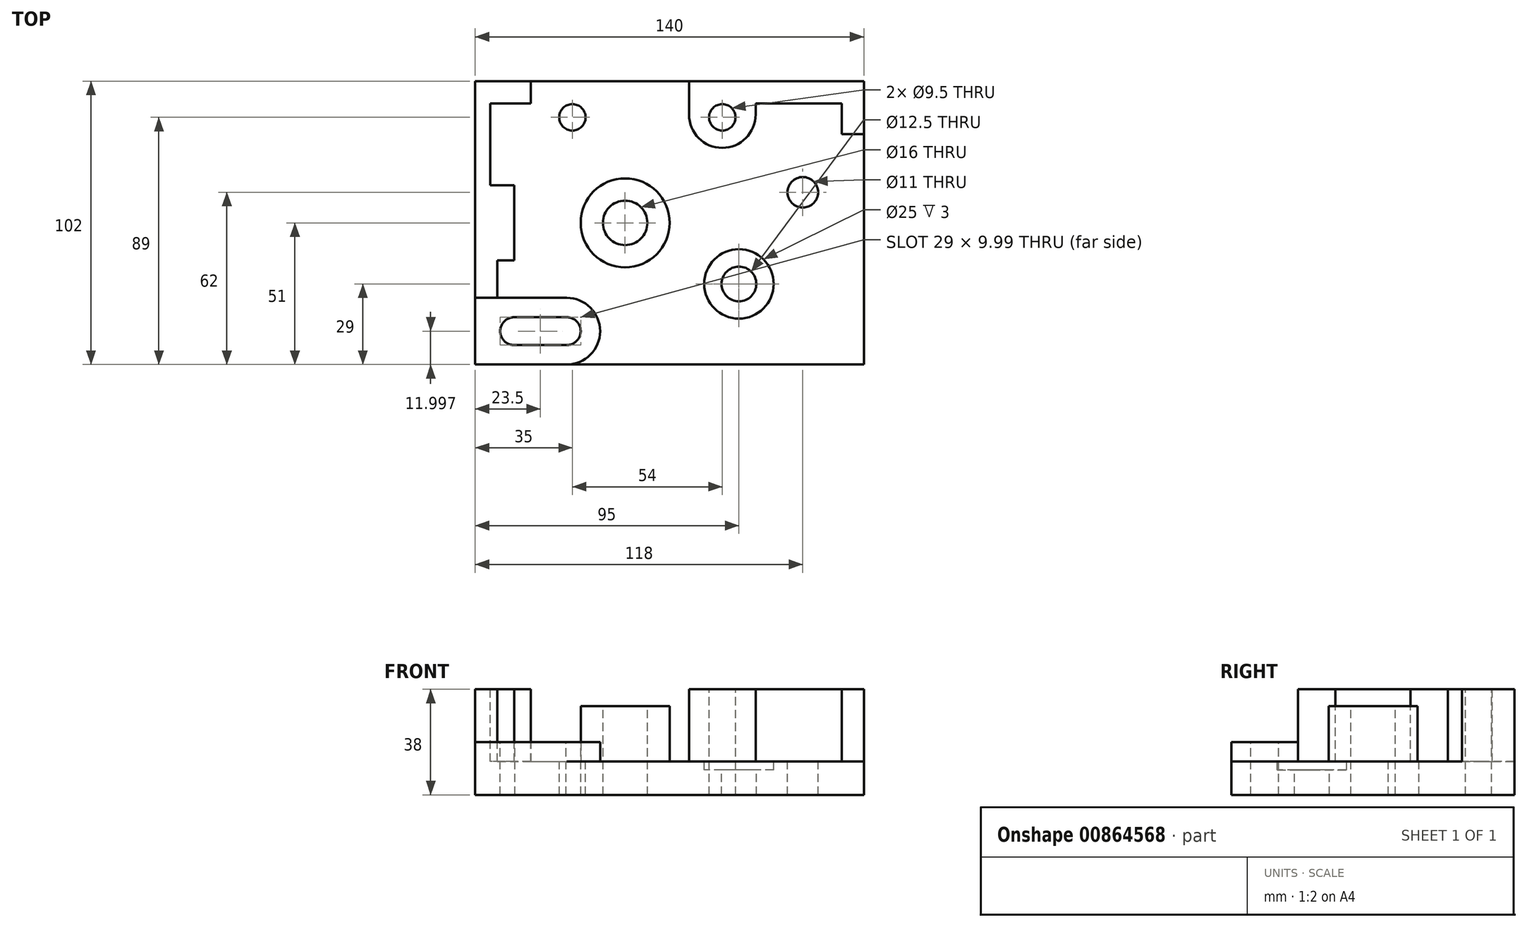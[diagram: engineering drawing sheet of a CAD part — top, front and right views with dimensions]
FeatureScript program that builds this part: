
annotation { "Feature Type Name" : "Feature", "Feature Type Description" : "" }
export const myFeature = defineFeature(function(context is Context, id is Id, definition is map)
    precondition{}
    {
        {
            var Q0;
            Q0=qCreatedBy(makeId("Front.planeOp"),FACE);
            var sketch = newSketch(context, id + "F0", { "sketchPlane" : qUnion([Q0])});
            skLineSegment(sketch, "E0.bottom", {"start": v(0, 0) * mm, "end": v(140, 0) * mm});
            skLineSegment(sketch, "E0.top", {"start": v(0, 38) * mm, "end": v(140, 38) * mm});
            skLineSegment(sketch, "E0.left", {"start": v(0, 0) * mm, "end": v(0, 38) * mm});
            skLineSegment(sketch, "E0.right", {"start": v(140, 0) * mm, "end": v(140, 38) * mm});
            skSolve(sketch);
        }
        {
            var Q0;
            Q0=qSketchRegion(id+"F0",true);
            extrude(context, id + "F1", {"entities" : qUnion([Q0]), "depth" : 102 * mm, "offsetDistance" : 25.4 * mm});
        }
        {
            var Q0;
            Q0=makeQuery(id+"F1.opExtrude","SWEPT_FACE",FACE,{"disambiguationData":[OSD([sQuery(id+"F0.wireOp",EDGE,"E0.top")])]});
            var sketch = newSketch(context, id + "F2", { "sketchPlane" : qUnion([Q0])});
            skCircle(sketch, "E1", {"center": v(35, -13) * mm, "radius": 4.75 * mm});
            skCircle(sketch, "E2", {"center": v(89, -13) * mm, "radius": 4.75 * mm});
            skSolve(sketch);
        }
        {
            var Q0;
            Q0=qSketchRegion(id+"F2",true);
            extrude(context, id + "F3", {"entities" : qUnion([Q0]), "operationType" : NewBodyOperationType.REMOVE, "oppositeDirection" : true, "depth" : 40 * mm, "offsetDistance" : 25.4 * mm});
        }
        {
            var Q0;
            Q0=makeQuery(id+"F1.opExtrude","SWEPT_FACE",FACE,{"disambiguationData":[OSD([sQuery(id+"F0.wireOp",EDGE,"E0.top")])]});
            var sketch = newSketch(context, id + "F4", { "sketchPlane" : qUnion([Q0])});
            skCircle(sketch, "E3", {"center": v(54, -51) * mm, "radius": 8 * mm});
            skSolve(sketch);
        }
        {
            var Q0;
            Q0=qSketchRegion(id+"F4",true);
            extrude(context, id + "F5", {"entities" : qUnion([Q0]), "operationType" : NewBodyOperationType.REMOVE, "oppositeDirection" : true, "depth" : 40 * mm, "offsetDistance" : 25.4 * mm});
        }
        {
            var Q0;
            Q0=makeQuery(id+"F1.opExtrude","SWEPT_FACE",FACE,{"disambiguationData":[OSD([sQuery(id+"F0.wireOp",EDGE,"E0.top")])]});
            var sketch = newSketch(context, id + "F6", { "sketchPlane" : qUnion([Q0])});
            skCircle(sketch, "E4", {"center": v(95, -73) * mm, "radius": 6.25 * mm});
            skSolve(sketch);
        }
        {
            var Q0;
            Q0=qSketchRegion(id+"F6",true);
            extrude(context, id + "F7", {"entities" : qUnion([Q0]), "operationType" : NewBodyOperationType.REMOVE, "oppositeDirection" : true, "depth" : 40 * mm, "offsetDistance" : 25.4 * mm});
        }
        {
            var Q0;
            Q0=makeQuery(id+"F1.opExtrude","SWEPT_FACE",FACE,{"disambiguationData":[OSD([sQuery(id+"F0.wireOp",EDGE,"E0.top")])]});
            var sketch = newSketch(context, id + "F8", { "sketchPlane" : qUnion([Q0])});
            skCircle(sketch, "E5", {"center": v(118, -40) * mm, "radius": 5.5 * mm});
            skSolve(sketch);
        }
        {
            var Q0;
            Q0=qSketchRegion(id+"F8",true);
            extrude(context, id + "F9", {"entities" : qUnion([Q0]), "operationType" : NewBodyOperationType.REMOVE, "oppositeDirection" : true, "depth" : 40 * mm, "offsetDistance" : 25.4 * mm});
        }
        {
            var Q0;
            Q0=makeQuery(id+"F1.opExtrude","CAP_FACE",FACE,{"disambiguationData":[OSD([sQuery(id+"F0.wireOp",EDGE,"E0.bottom"),sQuery(id+"F0.wireOp",EDGE,"E0.top"),sQuery(id+"F0.wireOp",EDGE,"E0.left"),sQuery(id+"F0.wireOp",EDGE,"E0.right")])],"isStart":false});
            var sketch = newSketch(context, id + "F10", { "sketchPlane" : qUnion([Q0])});
            skLineSegment(sketch, "E6.bottom", {"start": v(0, 38) * mm, "end": v(140, 38) * mm});
            skLineSegment(sketch, "E6.top", {"start": v(0, 12) * mm, "end": v(140, 12) * mm});
            skLineSegment(sketch, "E6.left", {"start": v(0, 38) * mm, "end": v(0, 12) * mm});
            skLineSegment(sketch, "E6.right", {"start": v(140, 38) * mm, "end": v(140, 12) * mm});
            skSolve(sketch);
        }
        {
            var Q0;
            Q0=qSketchRegion(id+"F10",true);
            extrude(context, id + "F11", {"entities" : qUnion([Q0]), "operationType" : NewBodyOperationType.REMOVE, "oppositeDirection" : true, "depth" : 102 * mm, "offsetDistance" : 25.4 * mm});
        }
        {
            var Q0;
            Q0=makeQuery(id+"F11.boolean.opBoolean","COPY",FACE,{"derivedFrom":makeQuery(id+"F11.opExtrude","SWEPT_FACE",FACE,{"disambiguationData":[OSD([sQuery(id+"F10.wireOp",EDGE,"E6.top")])]})});
            var sketch = newSketch(context, id + "F12", { "sketchPlane" : qUnion([Q0])});
            skCircle(sketch, "E7", {"center": v(54, -51) * mm, "radius": 16 * mm});
            skSolve(sketch);
        }
        {
            var Q0;
            Q0=qSketchRegion(id+"F12",true);
            extrude(context, id + "F13", {"entities" : qUnion([Q0]), "operationType" : NewBodyOperationType.ADD, "depth" : 26 * mm, "offsetDistance" : 25.4 * mm});
        }
        {
            var Q0;
            Q0=makeQuery(id+"F13.opExtrude","CAP_FACE",FACE,{"disambiguationData":[OSD([sQuery(id+"F12.wireOp",EDGE,"E7")])],"isStart":false});
            var sketch = newSketch(context, id + "F14", { "sketchPlane" : qUnion([Q0])});
            skCircle(sketch, "E8", {"center": v(54, -51) * mm, "radius": 8 * mm});
            skSolve(sketch);
        }
        {
            var Q0;
            Q0=qSketchRegion(id+"F14",true);
            extrude(context, id + "F15", {"entities" : qUnion([Q0]), "operationType" : NewBodyOperationType.REMOVE, "oppositeDirection" : true, "depth" : 26 * mm, "offsetDistance" : 25.4 * mm});
        }
        {
            var Q0;
            Q0=makeQuery(id+"F11.boolean.opBoolean","COPY",FACE,{"derivedFrom":makeQuery(id+"F11.opExtrude","SWEPT_FACE",FACE,{"disambiguationData":[OSD([sQuery(id+"F10.wireOp",EDGE,"E6.top")])]})});
            var sketch = newSketch(context, id + "F16", { "sketchPlane" : qUnion([Q0])});
            skLineSegment(sketch, "E9.bottom", {"start": v(0, -102) * mm, "end": v(45, -102) * mm});
            skLineSegment(sketch, "E9.top", {"start": v(0, -78) * mm, "end": v(45, -78) * mm});
            skLineSegment(sketch, "E9.left", {"start": v(0, -102) * mm, "end": v(0, -78) * mm});
            skLineSegment(sketch, "E9.right", {"start": v(45, -102) * mm, "end": v(45, -78) * mm});
            skSolve(sketch);
        }
        {
            var Q0;
            Q0=qSketchRegion(id+"F16",true);
            extrude(context, id + "F17", {"entities" : qUnion([Q0]), "operationType" : NewBodyOperationType.ADD, "depth" : 7 * mm, "offsetDistance" : 25.4 * mm});
        }
        {
            var Q0;
            Q0=makeQuery(id+"F17.opExtrude","SWEPT_EDGE",EDGE,{"disambiguationData":[OSD([sQuery(id+"F16.wireOp",EDGE,"E9.top"),sQuery(id+"F16.wireOp",EDGE,"E9.right")])]});
            fillet(context, id + "F18", {"entities" : qUnion([Q0]), "radius" : 12 * mm, "tangentPropagation" : true, "allowEdgeOverflow" : false});
        }
        {
            var Q0;
            Q0=makeQuery(id+"F17.opExtrude","SWEPT_EDGE",EDGE,{"disambiguationData":[OSD([sQuery(id+"F10.wireOp",EDGE,"E6.top"),sQuery(id+"F16.wireOp",EDGE,"E9.bottom"),sQuery(id+"F16.wireOp",EDGE,"E9.right")])]});
            fillet(context, id + "F19", {"entities" : qUnion([Q0]), "radius" : 12 * mm, "tangentPropagation" : true, "allowEdgeOverflow" : false});
        }
        {
            var Q0;
            Q0=makeQuery(id+"F11.boolean.opBoolean","COPY",FACE,{"derivedFrom":makeQuery(id+"F11.opExtrude","SWEPT_FACE",FACE,{"disambiguationData":[OSD([sQuery(id+"F10.wireOp",EDGE,"E6.top")])]})});
            var sketch = newSketch(context, id + "F20", { "sketchPlane" : qUnion([Q0])});
            skLineSegment(sketch, "E10.bottom", {"start": v(0, -78) * mm, "end": v(20, -78) * mm});
            skLineSegment(sketch, "E10.top", {"start": v(0, 0) * mm, "end": v(20, 0) * mm});
            skLineSegment(sketch, "E10.left", {"start": v(0, -78) * mm, "end": v(0, 0) * mm});
            skLineSegment(sketch, "E10.right", {"start": v(20, -78) * mm, "end": v(20, 0) * mm});
            skSolve(sketch);
        }
        {
            var Q0;
            Q0=qSketchRegion(id+"F20",true);
            extrude(context, id + "F21", {"entities" : qUnion([Q0]), "operationType" : NewBodyOperationType.ADD, "depth" : 26 * mm, "offsetDistance" : 25.4 * mm});
        }
        {
            var Q0;
            Q0=makeQuery(id+"F11.boolean.opBoolean","COPY",FACE,{"derivedFrom":makeQuery(id+"F11.opExtrude","SWEPT_FACE",FACE,{"disambiguationData":[OSD([sQuery(id+"F10.wireOp",EDGE,"E6.top")])]})});
            var sketch = newSketch(context, id + "F22", { "sketchPlane" : qUnion([Q0])});
            skLineSegment(sketch, "E11.bottom", {"start": v(140, 0) * mm, "end": v(77, 0) * mm});
            skLineSegment(sketch, "E11.top", {"start": v(140, -24) * mm, "end": v(77, -24) * mm});
            skLineSegment(sketch, "E11.left", {"start": v(140, 0) * mm, "end": v(140, -24) * mm});
            skLineSegment(sketch, "E11.right", {"start": v(77, 0) * mm, "end": v(77, -24) * mm});
            skSolve(sketch);
        }
        {
            var Q0;
            Q0=qSketchRegion(id+"F22",true);
            extrude(context, id + "F23", {"entities" : qUnion([Q0]), "operationType" : NewBodyOperationType.ADD, "depth" : 26 * mm, "offsetDistance" : 25.4 * mm});
        }
        {
            var Q0;
            Q0=makeQuery(id+"F1.opExtrude","SWEPT_FACE",FACE,{"disambiguationData":[OSD([sQuery(id+"F0.wireOp",EDGE,"E0.bottom")])]});
            var sketch = newSketch(context, id + "F24", { "sketchPlane" : qUnion([Q0])});
            skCircle(sketch, "E12", {"center": v(89, 13) * mm, "radius": 4.75 * mm});
            skSolve(sketch);
        }
        {
            var Q0;
            Q0=qSketchRegion(id+"F24",true);
            extrude(context, id + "F25", {"entities" : qUnion([Q0]), "operationType" : NewBodyOperationType.REMOVE, "oppositeDirection" : true, "depth" : 38 * mm, "offsetDistance" : 25.4 * mm});
        }
        {
            var Q0;
            Q0=makeQuery(id+"F23.opExtrude","SWEPT_EDGE",EDGE,{"disambiguationData":[OSD([sQuery(id+"F22.wireOp",EDGE,"E11.top"),sQuery(id+"F22.wireOp",EDGE,"E11.right")])]});
            fillet(context, id + "F26", {"entities" : qUnion([Q0]), "radius" : 12 * mm, "tangentPropagation" : true, "allowEdgeOverflow" : false});
        }
        {
            var Q0;
            Q0=makeQuery(id+"F17.opExtrude","CAP_FACE",FACE,{"disambiguationData":[OSD([sQuery(id+"F16.wireOp",EDGE,"E9.bottom"),sQuery(id+"F16.wireOp",EDGE,"E9.top"),sQuery(id+"F16.wireOp",EDGE,"E9.left"),sQuery(id+"F16.wireOp",EDGE,"E9.right")])],"isStart":false});
            var sketch = newSketch(context, id + "F27", { "sketchPlane" : qUnion([Q0])});
            skCircle(sketch, "E13", {"center": v(14, -90) * mm, "radius": 5 * mm});
            skCircle(sketch, "E14", {"center": v(33, -90) * mm, "radius": 5 * mm});
            skSolve(sketch);
        }
        {
            var Q0;
            Q0=qSketchRegion(id+"F27",true);
            extrude(context, id + "F28", {"entities" : qUnion([Q0]), "operationType" : NewBodyOperationType.REMOVE, "oppositeDirection" : true, "depth" : 40 * mm, "offsetDistance" : 25.4 * mm});
        }
        {
            var Q0;
            Q0=makeQuery(id+"F17.opExtrude","CAP_FACE",FACE,{"disambiguationData":[OSD([sQuery(id+"F16.wireOp",EDGE,"E9.bottom"),sQuery(id+"F16.wireOp",EDGE,"E9.top"),sQuery(id+"F16.wireOp",EDGE,"E9.left"),sQuery(id+"F16.wireOp",EDGE,"E9.right")])],"isStart":false});
            var sketch = newSketch(context, id + "F29", { "sketchPlane" : qUnion([Q0])});
            skLineSegment(sketch, "E15.bottom", {"start": v(14, -90) * mm, "end": v(33.25, -90) * mm});
            skLineSegment(sketch, "E15.top", {"start": v(14, -85) * mm, "end": v(33.25, -85) * mm});
            skLineSegment(sketch, "E15.left", {"start": v(14, -90) * mm, "end": v(14, -85) * mm});
            skLineSegment(sketch, "E15.right", {"start": v(33.25, -90) * mm, "end": v(33.25, -85) * mm});
            skSolve(sketch);
        }
        {
            var Q0;
            {var subQ0=sQuery(id+"F29.wireOp",EDGE,"E15.bottom");var subQ1=makeQuery(id+"F28.boolean.opBoolean","COPY",EDGE,{"derivedFrom":makeQuery(id+"F28.opExtrude","CAP_EDGE",EDGE,{"disambiguationData":[OSD([sQuery(id+"F27.wireOp",EDGE,"E13")])],"isStart":true})});var subQ2=makeQuery(id+"F29.imprint","INTERSECT",VERTEX,{"derivedFrom":[subQ1,subQ0]});Q0=makeQuery(id+"F29.imprint","IMPRINT",FACE,{"disambiguationData":[TD([[makeQuery(id+"F29.imprint","IMPRINT",EDGE,{"disambiguationData":[TD([[subQ2,-1.0]])],"derivedFrom":subQ0}),1.0]])]});}
            extrude(context, id + "F30", {"entities" : qUnion([Q0]), "operationType" : NewBodyOperationType.REMOVE, "oppositeDirection" : true, "depth" : 40 * mm, "offsetDistance" : 25.4 * mm});
        }
        {
            var Q0;
            Q0=makeQuery(id+"F17.opExtrude","CAP_FACE",FACE,{"disambiguationData":[OSD([sQuery(id+"F16.wireOp",EDGE,"E9.bottom"),sQuery(id+"F16.wireOp",EDGE,"E9.top"),sQuery(id+"F16.wireOp",EDGE,"E9.left"),sQuery(id+"F16.wireOp",EDGE,"E9.right")])],"isStart":false});
            var sketch = newSketch(context, id + "F31", { "sketchPlane" : qUnion([Q0])});
            skLineSegment(sketch, "E16.bottom", {"start": v(14, -90) * mm, "end": v(33, -90) * mm});
            skLineSegment(sketch, "E16.top", {"start": v(14, -95) * mm, "end": v(33, -95) * mm});
            skLineSegment(sketch, "E16.left", {"start": v(14, -90) * mm, "end": v(14, -95) * mm});
            skLineSegment(sketch, "E16.right", {"start": v(33, -90) * mm, "end": v(33, -95) * mm});
            skSolve(sketch);
        }
        {
            var Q0;
            Q0=qSketchRegion(id+"F31",true);
            extrude(context, id + "F32", {"entities" : qUnion([Q0]), "operationType" : NewBodyOperationType.REMOVE, "oppositeDirection" : true, "depth" : 40 * mm, "offsetDistance" : 25.4 * mm});
        }
        {
            var Q0;
            Q0=makeQuery(id+"F23.opExtrude","CAP_FACE",FACE,{"disambiguationData":[OSD([sQuery(id+"F22.wireOp",EDGE,"E11.bottom"),sQuery(id+"F22.wireOp",EDGE,"E11.top"),sQuery(id+"F22.wireOp",EDGE,"E11.left"),sQuery(id+"F22.wireOp",EDGE,"E11.right")])],"isStart":false});
            var sketch = newSketch(context, id + "F33", { "sketchPlane" : qUnion([Q0])});
            skLineSegment(sketch, "E17.bottom", {"start": v(132, -24) * mm, "end": v(101, -24) * mm});
            skLineSegment(sketch, "E17.top", {"start": v(132, -8) * mm, "end": v(101, -8) * mm});
            skLineSegment(sketch, "E17.left", {"start": v(132, -24) * mm, "end": v(132, -8) * mm});
            skLineSegment(sketch, "E17.right", {"start": v(101, -24) * mm, "end": v(101, -8) * mm});
            skSolve(sketch);
        }
        {
            var Q0;
            Q0=makeQuery(id+"F33.imprint","IMPRINT",FACE,{"disambiguationData":[TD([[makeQuery(id+"F33.imprint","IMPRINT",EDGE,{"derivedFrom":sQuery(id+"F33.wireOp",EDGE,"E17.bottom")}),-1.0]])]});
            extrude(context, id + "F34", {"entities" : qUnion([Q0]), "operationType" : NewBodyOperationType.REMOVE, "oppositeDirection" : true, "depth" : 26 * mm, "offsetDistance" : 25.4 * mm});
        }
        {
            var Q0;
            Q0=makeQuery(id+"F34.boolean.opBoolean","COPY",EDGE,{"derivedFrom":makeQuery(id+"F34.opExtrude","SWEPT_EDGE",EDGE,{"disambiguationData":[OSD([sQuery(id+"F22.wireOp",EDGE,"E11.top"),sQuery(id+"F33.wireOp",EDGE,"E17.bottom"),sQuery(id+"F33.wireOp",EDGE,"E17.right")])]})});
            fillet(context, id + "F35", {"entities" : qUnion([Q0]), "radius" : 12 * mm, "tangentPropagation" : true, "allowEdgeOverflow" : false});
        }
        {
            var Q0;
            Q0=makeQuery(id+"F23.opExtrude","CAP_FACE",FACE,{"disambiguationData":[OSD([sQuery(id+"F22.wireOp",EDGE,"E11.bottom"),sQuery(id+"F22.wireOp",EDGE,"E11.top"),sQuery(id+"F22.wireOp",EDGE,"E11.left"),sQuery(id+"F22.wireOp",EDGE,"E11.right")])],"isStart":false});
            var sketch = newSketch(context, id + "F36", { "sketchPlane" : qUnion([Q0])});
            skLineSegment(sketch, "E18.bottom", {"start": v(132, -24) * mm, "end": v(140, -24) * mm});
            skLineSegment(sketch, "E18.top", {"start": v(132, -19) * mm, "end": v(140, -19) * mm});
            skLineSegment(sketch, "E18.left", {"start": v(132, -24) * mm, "end": v(132, -19) * mm});
            skLineSegment(sketch, "E18.right", {"start": v(140, -24) * mm, "end": v(140, -19) * mm});
            skSolve(sketch);
        }
        {
            var Q0;
            Q0=qSketchRegion(id+"F36",true);
            extrude(context, id + "F37", {"entities" : qUnion([Q0]), "operationType" : NewBodyOperationType.REMOVE, "oppositeDirection" : true, "depth" : 26 * mm, "offsetDistance" : 25.4 * mm});
        }
        {
            var Q0;
            Q0=makeQuery(id+"F13.opExtrude","CAP_FACE",FACE,{"disambiguationData":[OSD([sQuery(id+"F12.wireOp",EDGE,"E7")])],"isStart":false});
            var sketch = newSketch(context, id + "F38", { "sketchPlane" : qUnion([Q0])});
            skCircle(sketch, "E19", {"center": v(54, -51) * mm, "radius": 16 * mm});
            skSolve(sketch);
        }
        {
            var Q0;
            Q0=qSketchRegion(id+"F38",true);
            extrude(context, id + "F39", {"entities" : qUnion([Q0]), "operationType" : NewBodyOperationType.REMOVE, "oppositeDirection" : true, "depth" : 6 * mm, "offsetDistance" : 25.4 * mm});
        }
        {
            var Q0;
            Q0=makeQuery(id+"F21.opExtrude","CAP_FACE",FACE,{"disambiguationData":[OSD([sQuery(id+"F20.wireOp",EDGE,"E10.bottom"),sQuery(id+"F20.wireOp",EDGE,"E10.top"),sQuery(id+"F20.wireOp",EDGE,"E10.left"),sQuery(id+"F20.wireOp",EDGE,"E10.right")])],"isStart":false});
            var sketch = newSketch(context, id + "F40", { "sketchPlane" : qUnion([Q0])});
            skLineSegment(sketch, "E20.bottom", {"start": v(20, -78) * mm, "end": v(14, -78) * mm});
            skLineSegment(sketch, "E20.top", {"start": v(20, -3.85) * mm, "end": v(14, -3.85) * mm});
            skLineSegment(sketch, "E20.left", {"start": v(20, -78) * mm, "end": v(20, -3.85) * mm});
            skLineSegment(sketch, "E20.right", {"start": v(14, -78) * mm, "end": v(14, -3.85) * mm});
            skSolve(sketch);
        }
        {
            var Q0;
            Q0=qSketchRegion(id+"F40",true);
            extrude(context, id + "F41", {"entities" : qUnion([Q0]), "operationType" : NewBodyOperationType.REMOVE, "oppositeDirection" : true, "depth" : 26 * mm, "offsetDistance" : 25.4 * mm});
        }
        {
            var Q0;
            Q0=makeQuery(id+"F41.boolean.opBoolean","MERGE",FACE,{"derivedFrom":[makeQuery(id+"F37.boolean.opBoolean","MERGE",FACE,{"derivedFrom":[makeQuery(id+"F34.boolean.opBoolean","MERGE",FACE,{"derivedFrom":[makeQuery(id+"F11.boolean.opBoolean","COPY",FACE,{"derivedFrom":makeQuery(id+"F11.opExtrude","SWEPT_FACE",FACE,{"disambiguationData":[OSD([sQuery(id+"F10.wireOp",EDGE,"E6.top")])]})}),makeQuery(id+"F34.opExtrude","CAP_FACE",FACE,{"disambiguationData":[OSD([sQuery(id+"F33.wireOp",EDGE,"E17.bottom"),sQuery(id+"F33.wireOp",EDGE,"E17.top"),sQuery(id+"F33.wireOp",EDGE,"E17.left"),sQuery(id+"F33.wireOp",EDGE,"E17.right")])],"isStart":false})]}),makeQuery(id+"F37.opExtrude","CAP_FACE",FACE,{"disambiguationData":[OSD([sQuery(id+"F36.wireOp",EDGE,"E18.bottom"),sQuery(id+"F36.wireOp",EDGE,"E18.top"),sQuery(id+"F36.wireOp",EDGE,"E18.left"),sQuery(id+"F36.wireOp",EDGE,"E18.right")])],"isStart":false})]}),makeQuery(id+"F41.opExtrude","CAP_FACE",FACE,{"disambiguationData":[OSD([sQuery(id+"F40.wireOp",EDGE,"E20.bottom"),sQuery(id+"F40.wireOp",EDGE,"E20.top"),sQuery(id+"F40.wireOp",EDGE,"E20.left"),sQuery(id+"F40.wireOp",EDGE,"E20.right")])],"isStart":false})]});
            var sketch = newSketch(context, id + "F42", { "sketchPlane" : qUnion([Q0])});
            skLineSegment(sketch, "E21.bottom", {"start": v(14, -3.85) * mm, "end": v(20, -3.85) * mm});
            skLineSegment(sketch, "E21.top", {"start": v(14, -7.85) * mm, "end": v(20, -7.85) * mm});
            skLineSegment(sketch, "E21.left", {"start": v(14, -3.85) * mm, "end": v(14, -7.85) * mm});
            skLineSegment(sketch, "E21.right", {"start": v(20, -3.85) * mm, "end": v(20, -7.85) * mm});
            skSolve(sketch);
        }
        {
            var Q0;
            Q0=qSketchRegion(id+"F42",true);
            extrude(context, id + "F43", {"entities" : qUnion([Q0]), "operationType" : NewBodyOperationType.ADD, "depth" : 26 * mm, "offsetDistance" : 25.4 * mm});
        }
        {
            var Q0;
            Q0=makeQuery(id+"F43.boolean.opBoolean","MERGE",FACE,{"derivedFrom":[makeQuery(id+"F21.opExtrude","CAP_FACE",FACE,{"disambiguationData":[OSD([sQuery(id+"F20.wireOp",EDGE,"E10.bottom"),sQuery(id+"F20.wireOp",EDGE,"E10.top"),sQuery(id+"F20.wireOp",EDGE,"E10.left"),sQuery(id+"F20.wireOp",EDGE,"E10.right")])],"isStart":false}),makeQuery(id+"F43.opExtrude","CAP_FACE",FACE,{"disambiguationData":[OSD([sQuery(id+"F42.wireOp",EDGE,"E21.bottom"),sQuery(id+"F42.wireOp",EDGE,"E21.top"),sQuery(id+"F42.wireOp",EDGE,"E21.left"),sQuery(id+"F42.wireOp",EDGE,"E21.right")])],"isStart":false})]});
            var sketch = newSketch(context, id + "F44", { "sketchPlane" : qUnion([Q0])});
            skLineSegment(sketch, "E22.bottom", {"start": v(14, -78) * mm, "end": v(8, -78) * mm});
            skLineSegment(sketch, "E22.top", {"start": v(14, -64.5) * mm, "end": v(8, -64.5) * mm});
            skLineSegment(sketch, "E22.left", {"start": v(14, -78) * mm, "end": v(14, -64.5) * mm});
            skLineSegment(sketch, "E22.right", {"start": v(8, -78) * mm, "end": v(8, -64.5) * mm});
            skSolve(sketch);
        }
        {
            var Q0;
            Q0=qSketchRegion(id+"F44",true);
            extrude(context, id + "F45", {"entities" : qUnion([Q0]), "operationType" : NewBodyOperationType.REMOVE, "oppositeDirection" : true, "depth" : 26 * mm, "offsetDistance" : 25.4 * mm});
        }
        {
            var Q0;
            Q0=makeQuery(id+"F43.boolean.opBoolean","MERGE",FACE,{"derivedFrom":[makeQuery(id+"F21.opExtrude","CAP_FACE",FACE,{"disambiguationData":[OSD([sQuery(id+"F20.wireOp",EDGE,"E10.bottom"),sQuery(id+"F20.wireOp",EDGE,"E10.top"),sQuery(id+"F20.wireOp",EDGE,"E10.left"),sQuery(id+"F20.wireOp",EDGE,"E10.right")])],"isStart":false}),makeQuery(id+"F43.opExtrude","CAP_FACE",FACE,{"disambiguationData":[OSD([sQuery(id+"F42.wireOp",EDGE,"E21.bottom"),sQuery(id+"F42.wireOp",EDGE,"E21.top"),sQuery(id+"F42.wireOp",EDGE,"E21.left"),sQuery(id+"F42.wireOp",EDGE,"E21.right")])],"isStart":false})]});
            var sketch = newSketch(context, id + "F46", { "sketchPlane" : qUnion([Q0])});
            skLineSegment(sketch, "E23", {"start": v(14, -64.5) * mm, "end": v(14, -37.5) * mm});
            skLineSegment(sketch, "E24.bottom", {"start": v(14, -37.5) * mm, "end": v(5.42, -37.5) * mm});
            skLineSegment(sketch, "E24.top", {"start": v(14, -8) * mm, "end": v(5.42, -8) * mm});
            skLineSegment(sketch, "E24.left", {"start": v(14, -37.5) * mm, "end": v(14, -8) * mm});
            skLineSegment(sketch, "E24.right", {"start": v(5.42, -37.5) * mm, "end": v(5.42, -8) * mm});
            skSolve(sketch);
        }
        {
            var Q0;
            Q0=qSketchRegion(id+"F46",true);
            extrude(context, id + "F47", {"entities" : qUnion([Q0]), "operationType" : NewBodyOperationType.REMOVE, "oppositeDirection" : true, "depth" : 26 * mm, "offsetDistance" : 25.4 * mm});
        }
        {
            var Q0;
            Q0=makeQuery(id+"F43.boolean.opBoolean","MERGE",FACE,{"derivedFrom":[makeQuery(id+"F21.opExtrude","CAP_FACE",FACE,{"disambiguationData":[OSD([sQuery(id+"F20.wireOp",EDGE,"E10.bottom"),sQuery(id+"F20.wireOp",EDGE,"E10.top"),sQuery(id+"F20.wireOp",EDGE,"E10.left"),sQuery(id+"F20.wireOp",EDGE,"E10.right")])],"isStart":false}),makeQuery(id+"F43.opExtrude","CAP_FACE",FACE,{"disambiguationData":[OSD([sQuery(id+"F42.wireOp",EDGE,"E21.bottom"),sQuery(id+"F42.wireOp",EDGE,"E21.top"),sQuery(id+"F42.wireOp",EDGE,"E21.left"),sQuery(id+"F42.wireOp",EDGE,"E21.right")])],"isStart":false})]});
            var sketch = newSketch(context, id + "F48", { "sketchPlane" : qUnion([Q0])});
            skLineSegment(sketch, "E25.bottom", {"start": v(14, -8) * mm, "end": v(20, -8) * mm});
            skLineSegment(sketch, "E25.top", {"start": v(14, -7.85) * mm, "end": v(20, -7.85) * mm});
            skLineSegment(sketch, "E25.left", {"start": v(14, -8) * mm, "end": v(14, -7.85) * mm});
            skLineSegment(sketch, "E25.right", {"start": v(20, -8) * mm, "end": v(20, -7.85) * mm});
            skSolve(sketch);
        }
        {
            var Q0;
            Q0=qSketchRegion(id+"F48",true);
            extrude(context, id + "F49", {"entities" : qUnion([Q0]), "operationType" : NewBodyOperationType.ADD, "oppositeDirection" : true, "depth" : 26 * mm, "offsetDistance" : 25.4 * mm});
        }
        {
            var Q0;
            Q0=makeQuery(id+"F47.boolean.opBoolean","MERGE",FACE,{"derivedFrom":[makeQuery(id+"F45.boolean.opBoolean","MERGE",FACE,{"derivedFrom":[makeQuery(id+"F41.boolean.opBoolean","MERGE",FACE,{"derivedFrom":[makeQuery(id+"F37.boolean.opBoolean","MERGE",FACE,{"derivedFrom":[makeQuery(id+"F34.boolean.opBoolean","MERGE",FACE,{"derivedFrom":[makeQuery(id+"F11.boolean.opBoolean","COPY",FACE,{"derivedFrom":makeQuery(id+"F11.opExtrude","SWEPT_FACE",FACE,{"disambiguationData":[OSD([sQuery(id+"F10.wireOp",EDGE,"E6.top")])]})}),makeQuery(id+"F34.opExtrude","CAP_FACE",FACE,{"disambiguationData":[OSD([sQuery(id+"F33.wireOp",EDGE,"E17.bottom"),sQuery(id+"F33.wireOp",EDGE,"E17.top"),sQuery(id+"F33.wireOp",EDGE,"E17.left"),sQuery(id+"F33.wireOp",EDGE,"E17.right")])],"isStart":false})]}),makeQuery(id+"F37.opExtrude","CAP_FACE",FACE,{"disambiguationData":[OSD([sQuery(id+"F36.wireOp",EDGE,"E18.bottom"),sQuery(id+"F36.wireOp",EDGE,"E18.top"),sQuery(id+"F36.wireOp",EDGE,"E18.left"),sQuery(id+"F36.wireOp",EDGE,"E18.right")])],"isStart":false})]}),makeQuery(id+"F41.opExtrude","CAP_FACE",FACE,{"disambiguationData":[OSD([sQuery(id+"F40.wireOp",EDGE,"E20.bottom"),sQuery(id+"F40.wireOp",EDGE,"E20.top"),sQuery(id+"F40.wireOp",EDGE,"E20.left"),sQuery(id+"F40.wireOp",EDGE,"E20.right")])],"isStart":false})]}),makeQuery(id+"F45.opExtrude","CAP_FACE",FACE,{"disambiguationData":[OSD([sQuery(id+"F44.wireOp",EDGE,"E22.bottom"),sQuery(id+"F44.wireOp",EDGE,"E22.top"),sQuery(id+"F44.wireOp",EDGE,"E22.left"),sQuery(id+"F44.wireOp",EDGE,"E22.right")])],"isStart":false})]}),makeQuery(id+"F47.opExtrude","CAP_FACE",FACE,{"disambiguationData":[OSD([sQuery(id+"F46.wireOp",EDGE,"E24.bottom"),sQuery(id+"F46.wireOp",EDGE,"E24.top"),sQuery(id+"F46.wireOp",EDGE,"E24.left"),sQuery(id+"F46.wireOp",EDGE,"E24.right")])],"isStart":false})]});
            var sketch = newSketch(context, id + "F50", { "sketchPlane" : qUnion([Q0])});
            skCircle(sketch, "E26", {"center": v(95, -73) * mm, "radius": 12.5 * mm});
            skSolve(sketch);
        }
        {
            var Q0;
            Q0=qSketchRegion(id+"F50",true);
            extrude(context, id + "F51", {"entities" : qUnion([Q0]), "operationType" : NewBodyOperationType.REMOVE, "oppositeDirection" : true, "depth" : 3 * mm, "offsetDistance" : 25.4 * mm});
        }
    });
